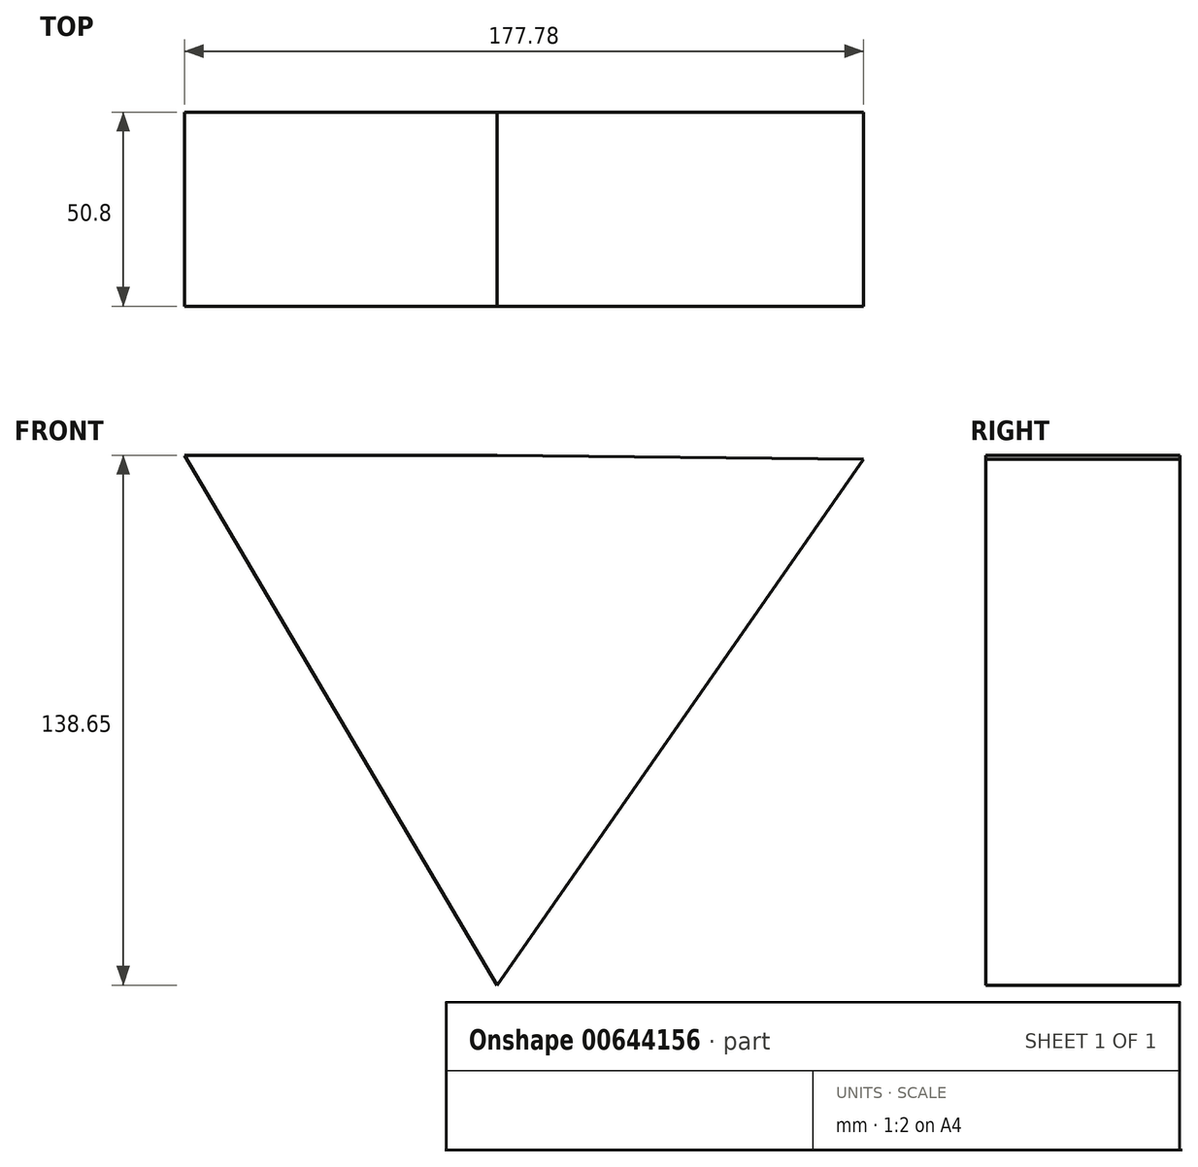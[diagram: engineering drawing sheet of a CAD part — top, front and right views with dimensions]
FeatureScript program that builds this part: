
annotation { "Feature Type Name" : "Feature", "Feature Type Description" : "" }
export const myFeature = defineFeature(function(context is Context, id is Id, definition is map)
    precondition{}
    {
        {
            var Q0;
            Q0=qCreatedBy(makeId("Front.planeOp"),FACE);
            var sketch = newSketch(context, id + "F0", { "sketchPlane" : qUnion([Q0])});
            skLineSegment(sketch, "E0", {"start": v(96.67, 0) * mm, "end": v(0, -138.65) * mm});
            skLineSegment(sketch, "E1", {"start": v(0, -138.65) * mm, "end": v(-81.82, 0) * mm});
            skLineSegment(sketch, "E2", {"start": v(-81.82, 0) * mm, "end": v(96.67, 0) * mm});
            skLineSegment(sketch, "E3", {"start": v(81.94, 77.37) * mm, "end": v(0, 0) * mm});
            skLineSegment(sketch, "E4", {"start": v(0, 0) * mm, "end": v(96, -1.02) * mm});
            skLineSegment(sketch, "E5", {"start": v(96, -1.02) * mm, "end": v(81.94, 77.37) * mm});
            skLineSegment(sketch, "E6", {"start": v(81.94, 77.37) * mm, "end": v(-81.82, 0) * mm});
            skLineSegment(sketch, "E7", {"start": v(-36.2, 56.43) * mm, "end": v(-58.47, 89.54) * mm});
            skLineSegment(sketch, "E8", {"start": v(-58.47, 89.54) * mm, "end": v(-81.82, 0) * mm});
            skLineSegment(sketch, "E9", {"start": v(81.94, 77.37) * mm, "end": v(-36.2, 56.43) * mm});
            skSolve(sketch);
        }
        {
            var Q0;
            {var subQ0=sQuery(id+"F0.wireOp",EDGE,"E1");Q0=makeQuery(id+"F0.imprint","IMPRINT",FACE,{"disambiguationData":[TD([[makeQuery(id+"F0.imprint","IMPRINT",EDGE,{"derivedFrom":subQ0}),-1.0]])]});}
            extrude(context, id + "F1", {"entities" : qUnion([Q0]), "depth" : 25.4 * mm, "offsetDistance" : 25.4 * mm});
        }
        {
            var Q0;
            Q0=makeQuery(id+"F1.opExtrude","CAP_FACE",FACE,{"disambiguationData":[OSD([sQuery(id+"F0.wireOp",EDGE,"E0"),sQuery(id+"F0.wireOp",EDGE,"E1"),sQuery(id+"F0.wireOp",EDGE,"E2"),sQuery(id+"F0.wireOp",EDGE,"E4")])],"isStart":true});
            extrude(context, id + "F2", {"entities" : qUnion([Q0]), "operationType" : NewBodyOperationType.ADD, "depth" : 25.4 * mm, "offsetDistance" : 25.4 * mm});
        }
    });
